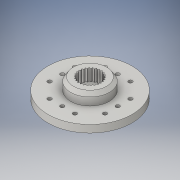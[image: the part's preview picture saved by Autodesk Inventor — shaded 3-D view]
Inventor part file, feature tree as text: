
AUTODESK INVENTOR PART (.ipt)
format: ipt  version: 2016 (Build 200138000, 138)  size: 290,816 bytes
history: native  units: mm
features: extrude x7, sketch x7, other x1, chamfer x1, pattern_circular x1
ambient origin geometry x8: Origin, YZ Plane, XZ Plane, XY Plane, X Axis, Y Axis, Z Axis, Center Point
bodies: Body1 (feature_tree)
feature tree (17):
  other  "Sólido1"
  extrude  "Extrusión1"  Depth=1.0mm
  extrude  "Extrusión2"  Depth=7.1mm
  chamfer  "Chaflán1"  Distance=40.0mm Angle=360.0deg
  extrude  "Extrusión4"  Depth=1.9mm
  extrude  "Extrusión5"  Depth=3.0mm
  extrude  "Extrusión7"  Depth=0.5mm
  pattern_circular  "Patrón circular1"  [2 undecoded]
  extrude  "Extrusión8"  Depth=3.0mm
  extrude  "Extrusión9"  Depth=3.0mm
  sketch  "Boceto1"  dims[d0=21.5mm d1=1.0mm]
  sketch  "Boceto2"  dims[d2=6.5mm d4=7.1mm d5=40.0mm d7=360.0deg]
  sketch  "Boceto6"  dims[d9=1.9mm d10=0.0mm d11=9.9mm]
  sketch  "Boceto7"  dims[d12=3.0mm d13=0.0mm d18=0.7mm d19=2.0mm d20=9.599311mm]
  sketch  "Boceto9"  dims[d24=6.5mm d25=0.5mm]
  sketch  "Boceto10"  dims[d26=1.0mm d27=0.0mm]
  sketch  "Boceto11"  dims[d28=8.5mm d29=0.4mm d30=0.0mm d34=5.2mm d37=13.962634mm d38=0.525825mm d39=3.0mm d40=0.0mm d41=260.0mm d42=360.0deg d44=3.0mm d45=0.0mm d46=2.8mm d47=3.0mm d48=0.0mm]
note: 2 required parameter values undecoded (feature->parameter linkage not recoverable at this tier; creation-order binding heuristic only, values carry confidence <= 0.55)
